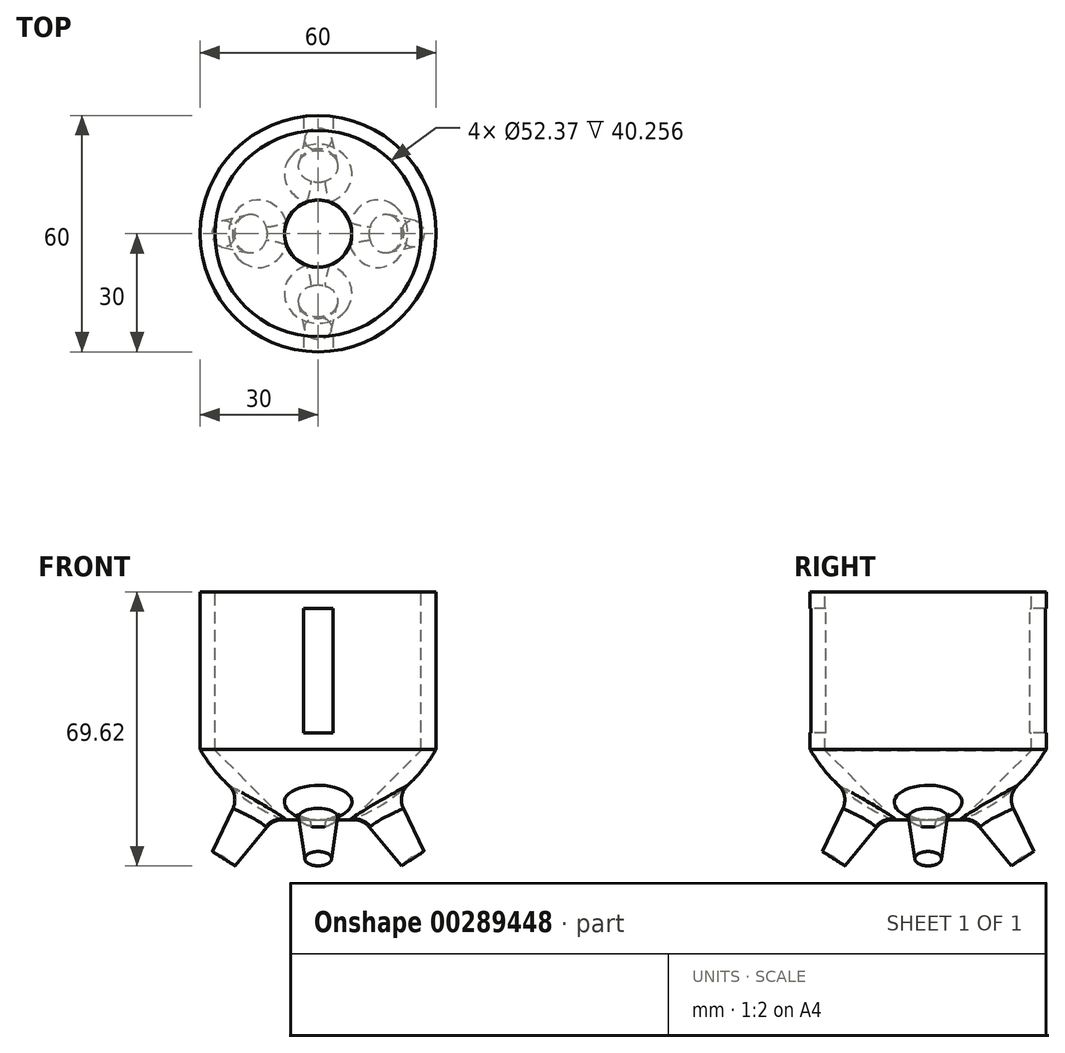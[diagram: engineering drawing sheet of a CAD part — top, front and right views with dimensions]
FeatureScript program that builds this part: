
annotation { "Feature Type Name" : "Feature", "Feature Type Description" : "" }
export const myFeature = defineFeature(function(context is Context, id is Id, definition is map)
    precondition{}
    {
        {
            var Q0;
            Q0=qCreatedBy(makeId("Front.planeOp"),FACE);
            var sketch = newSketch(context, id + "F0", { "sketchPlane" : qUnion([Q0])});
            skLineSegment(sketch, "E0", {"start": v(0, 29.43) * mm, "end": v(-30, 29.43) * mm});
            skLineSegment(sketch, "E1", {"start": v(-30, 29.43) * mm, "end": v(-30, 0) * mm});
            skLineSegment(sketch, "E2", {"start": v(0, 29.43) * mm, "end": v(0, -30.57) * mm});
            skLineSegment(sketch, "E3", {"start": v(-30, 0) * mm, "end": v(-30, -10.57) * mm});
            skArc(sketch, "E4", {"start": v(-30, -10.57) * mm, "mid": v(-17.32, -24.05) * mm, "end": v(0, -30.57) * mm});
            skSolve(sketch);
        }
        {
            var Q0;
            Q0=makeQuery(id+"F0.imprint","IMPRINT",FACE,{"disambiguationData":[TD([[makeQuery(id+"F0.imprint","IMPRINT",EDGE,{"derivedFrom":sQuery(id+"F0.wireOp",EDGE,"E0")}),1.0]])]});
            var Q1;
            Q1=sQuery(id+"F0.wireOp",EDGE,"E2");
            revolve(context, id + "F1", {"entities" : qUnion([Q0]), "axis" : qUnion([Q1]), "revolveType" : RevolveType.FULL});
        }
        {
            var Q0;
            Q0=qCreatedBy(makeId("Front.planeOp"),FACE);
            var sketch = newSketch(context, id + "F2", { "sketchPlane" : qUnion([Q0])});
            skLineSegment(sketch, "E5", {"start": v(-12.96, -21.03) * mm, "end": v(-7.88, -24.13) * mm});
            skLineSegment(sketch, "E6", {"start": v(-7.88, -24.13) * mm, "end": v(-21.13, -40.19) * mm});
            skLineSegment(sketch, "E7", {"start": v(-21.13, -40.19) * mm, "end": v(-23.78, -38) * mm});
            skLineSegment(sketch, "E8", {"start": v(-23.78, -38) * mm, "end": v(-12.96, -21.03) * mm});
            skSolve(sketch);
        }
        {
            var Q0;
            Q0=makeQuery(id+"F2.imprint","IMPRINT",FACE,{"disambiguationData":[TD([[makeQuery(id+"F2.imprint","IMPRINT",EDGE,{"derivedFrom":sQuery(id+"F2.wireOp",EDGE,"E5")}),-1.0]])]});
            var Q1;
            Q1=sQuery(id+"F2.wireOp",EDGE,"E8");
            revolve(context, id + "F3", {"operationType" : NewBodyOperationType.ADD, "entities" : qUnion([Q0]), "axis" : qUnion([Q1]), "revolveType" : RevolveType.FULL});
        }
        {
            var Q0;
            Q0=makeQuery(id+"F1.opRevolve","SWEPT_BODY",BODY,{"disambiguationData":[OSD([sQuery(id+"F0.wireOp",EDGE,"E0"),sQuery(id+"F0.wireOp",EDGE,"E1"),sQuery(id+"F0.wireOp",EDGE,"E2"),sQuery(id+"F0.wireOp",EDGE,"E3"),sQuery(id+"F0.wireOp",EDGE,"E4")])]});
            var Q1;
            Q1=makeQuery(id+"F1.opRevolve","SWEPT_EDGE",EDGE,{"disambiguationData":[OSD([sQuery(id+"F0.wireOp",EDGE,"E0"),sQuery(id+"F0.wireOp",EDGE,"E1")])]});
            circularPattern(context, id + "F4", {"entities" : qUnion([Q0]), "axis" : qUnion([Q1]), "angle" : 360 * degree, "instanceCount" : 4, "equalSpace" : true});
        }
        {
            var Q0;
            Q0=qCreatedBy(makeId("Front.planeOp"),FACE);
            var sketch = newSketch(context, id + "F5", { "sketchPlane" : qUnion([Q0])});
            skLineSegment(sketch, "E9", {"start": v(0, 29.43) * mm, "end": v(-26.19, 29.43) * mm});
            skLineSegment(sketch, "E10", {"start": v(-26.19, 29.43) * mm, "end": v(-26.19, -10.83) * mm});
            skLineSegment(sketch, "E11", {"start": v(-26.19, -10.83) * mm, "end": v(-3.54, -33.47) * mm});
            skLineSegment(sketch, "E12", {"start": v(-3.54, -33.47) * mm, "end": v(0, -33.47) * mm});
            skLineSegment(sketch, "E13", {"start": v(0, -33.47) * mm, "end": v(0, 29.43) * mm});
            skSolve(sketch);
        }
        {
            var Q0;
            Q0=makeQuery(id+"F5.imprint","IMPRINT",FACE,{"disambiguationData":[TD([[makeQuery(id+"F5.imprint","IMPRINT",EDGE,{"derivedFrom":sQuery(id+"F5.wireOp",EDGE,"E9")}),1.0]])]});
            var Q1;
            Q1=sQuery(id+"F5.wireOp",EDGE,"E13");
            revolve(context, id + "F6", {"operationType" : NewBodyOperationType.REMOVE, "entities" : qUnion([Q0]), "axis" : qUnion([Q1]), "revolveType" : RevolveType.FULL, "oppositeDirection" : true});
        }
        {
            var Q0;
            Q0=qCreatedBy(makeId("Front.planeOp"),FACE);
            var sketch = newSketch(context, id + "F7", { "sketchPlane" : qUnion([Q0])});
            skLineSegment(sketch, "E14", {"start": v(0, 29.43) * mm, "end": v(0, -10.57) * mm});
            skLineSegment(sketch, "E15.bottom", {"start": v(3.75, 25.23) * mm, "end": v(-3.75, 25.23) * mm});
            skLineSegment(sketch, "E15.top", {"start": v(3.75, -6.37) * mm, "end": v(-3.75, -6.37) * mm});
            skLineSegment(sketch, "E15.left", {"start": v(3.75, 25.23) * mm, "end": v(3.75, -6.37) * mm});
            skLineSegment(sketch, "E15.right", {"start": v(-3.75, 25.23) * mm, "end": v(-3.75, -6.37) * mm});
            skPoint(sketch, "E15.middle", {"position": v(0, 9.43) * mm});
            skSolve(sketch);
        }
        {
            var Q0;
            Q0 = qSketchRegion(id + "F7", true);
            extrude(context, id + "F8", {"entities" : qUnion([Q0]), "operationType" : NewBodyOperationType.REMOVE, "endBound" : BoundingType.THROUGH_ALL, "oppositeDirection" : true, "depth" : 25.4 * mm, "hasSecondDirection" : true, "secondDirectionBound" : SecondDirectionBoundingType.THROUGH_ALL, "secondDirectionOppositeDirection" : false, "secondDirectionDepth" : 25.4 * mm});
        }
        {
            var Q0;
            Q0=makeQuery(id+"F3.boolean.opBoolean","INTERSECT",EDGE,{"derivedFrom":[makeQuery(id+"F1.opRevolve","SWEPT_FACE",FACE,{"disambiguationData":[OSD([sQuery(id+"F0.wireOp",EDGE,"E4")])]}),makeQuery(id+"F3.opRevolve","SWEPT_FACE",FACE,{"disambiguationData":[OSD([sQuery(id+"F2.wireOp",EDGE,"E6")])]})]});
            var Q1;
            Q1=makeQuery(id+"F4.opPattern","COPY",EDGE,{"derivedFrom":makeQuery(id+"F3.boolean.opBoolean","INTERSECT",EDGE,{"derivedFrom":[makeQuery(id+"F1.opRevolve","SWEPT_FACE",FACE,{"disambiguationData":[OSD([sQuery(id+"F0.wireOp",EDGE,"E4")])]}),makeQuery(id+"F3.opRevolve","SWEPT_FACE",FACE,{"disambiguationData":[OSD([sQuery(id+"F2.wireOp",EDGE,"E6")])]})]}),"instanceName":"1"});
            var Q2;
            Q2=makeQuery(id+"F4.opPattern","COPY",EDGE,{"derivedFrom":makeQuery(id+"F3.boolean.opBoolean","INTERSECT",EDGE,{"derivedFrom":[makeQuery(id+"F1.opRevolve","SWEPT_FACE",FACE,{"disambiguationData":[OSD([sQuery(id+"F0.wireOp",EDGE,"E4")])]}),makeQuery(id+"F3.opRevolve","SWEPT_FACE",FACE,{"disambiguationData":[OSD([sQuery(id+"F2.wireOp",EDGE,"E6")])]})]}),"instanceName":"3"});
            var Q3;
            Q3=makeQuery(id+"F4.opPattern","COPY",EDGE,{"derivedFrom":makeQuery(id+"F3.boolean.opBoolean","INTERSECT",EDGE,{"derivedFrom":[makeQuery(id+"F1.opRevolve","SWEPT_FACE",FACE,{"disambiguationData":[OSD([sQuery(id+"F0.wireOp",EDGE,"E4")])]}),makeQuery(id+"F3.opRevolve","SWEPT_FACE",FACE,{"disambiguationData":[OSD([sQuery(id+"F2.wireOp",EDGE,"E6")])]})]}),"instanceName":"2"});
            fillet(context, id + "F9", {"entities" : qUnion([Q0, Q1, Q2, Q3]), "radius" : 5.08 * mm, "tangentPropagation" : true, "allowEdgeOverflow" : false});
        }
    });
